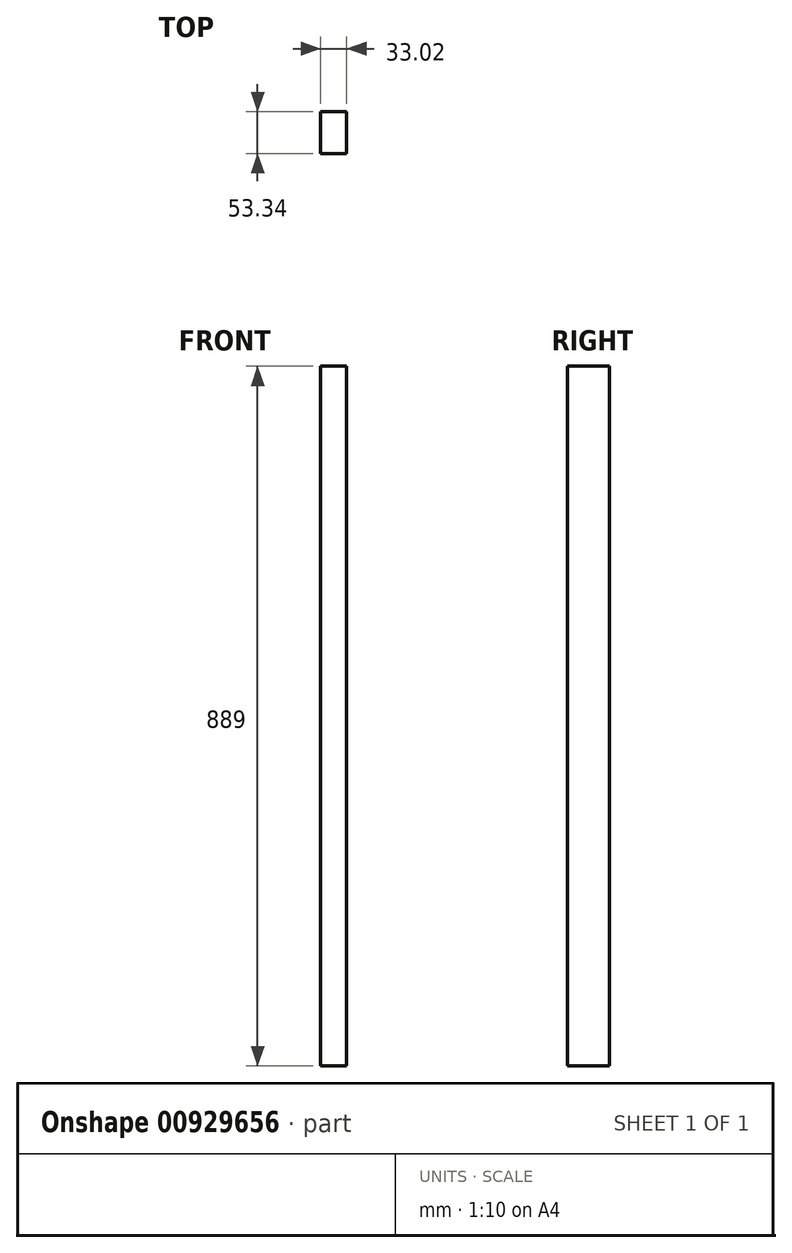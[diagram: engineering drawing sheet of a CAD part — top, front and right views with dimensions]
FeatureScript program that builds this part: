
annotation { "Feature Type Name" : "Feature", "Feature Type Description" : "" }
export const myFeature = defineFeature(function(context is Context, id is Id, definition is map)
    precondition{}
    {
        {
            var Q0;
            Q0=qCreatedBy(makeId("Right.planeOp"),FACE);
            var sketch = newSketch(context, id + "F0", { "sketchPlane" : qUnion([Q0])});
            skLineSegment(sketch, "E0.bottom", {"start": v(-1.6, 718.05) * mm, "end": v(-54.94, 718.05) * mm});
            skLineSegment(sketch, "E0.top", {"start": v(-1.6, -170.95) * mm, "end": v(-54.94, -170.95) * mm});
            skLineSegment(sketch, "E0.left", {"start": v(-1.6, 718.05) * mm, "end": v(-1.6, -170.95) * mm});
            skLineSegment(sketch, "E0.right", {"start": v(-54.94, 718.05) * mm, "end": v(-54.94, -170.95) * mm});
            skSolve(sketch);
        }
        {
            var Q0;
            Q0=makeQuery(id+"F0.imprint","IMPRINT",FACE,{"disambiguationData":[TD([[makeQuery(id+"F0.imprint","IMPRINT",EDGE,{"derivedFrom":sQuery(id+"F0.wireOp",EDGE,"E0.bottom")}),1.0]])]});
            extrude(context, id + "F1", {"entities" : qUnion([Q0]), "depth" : 33.02 * mm, "offsetDistance" : 25.4 * mm});
        }
    });
